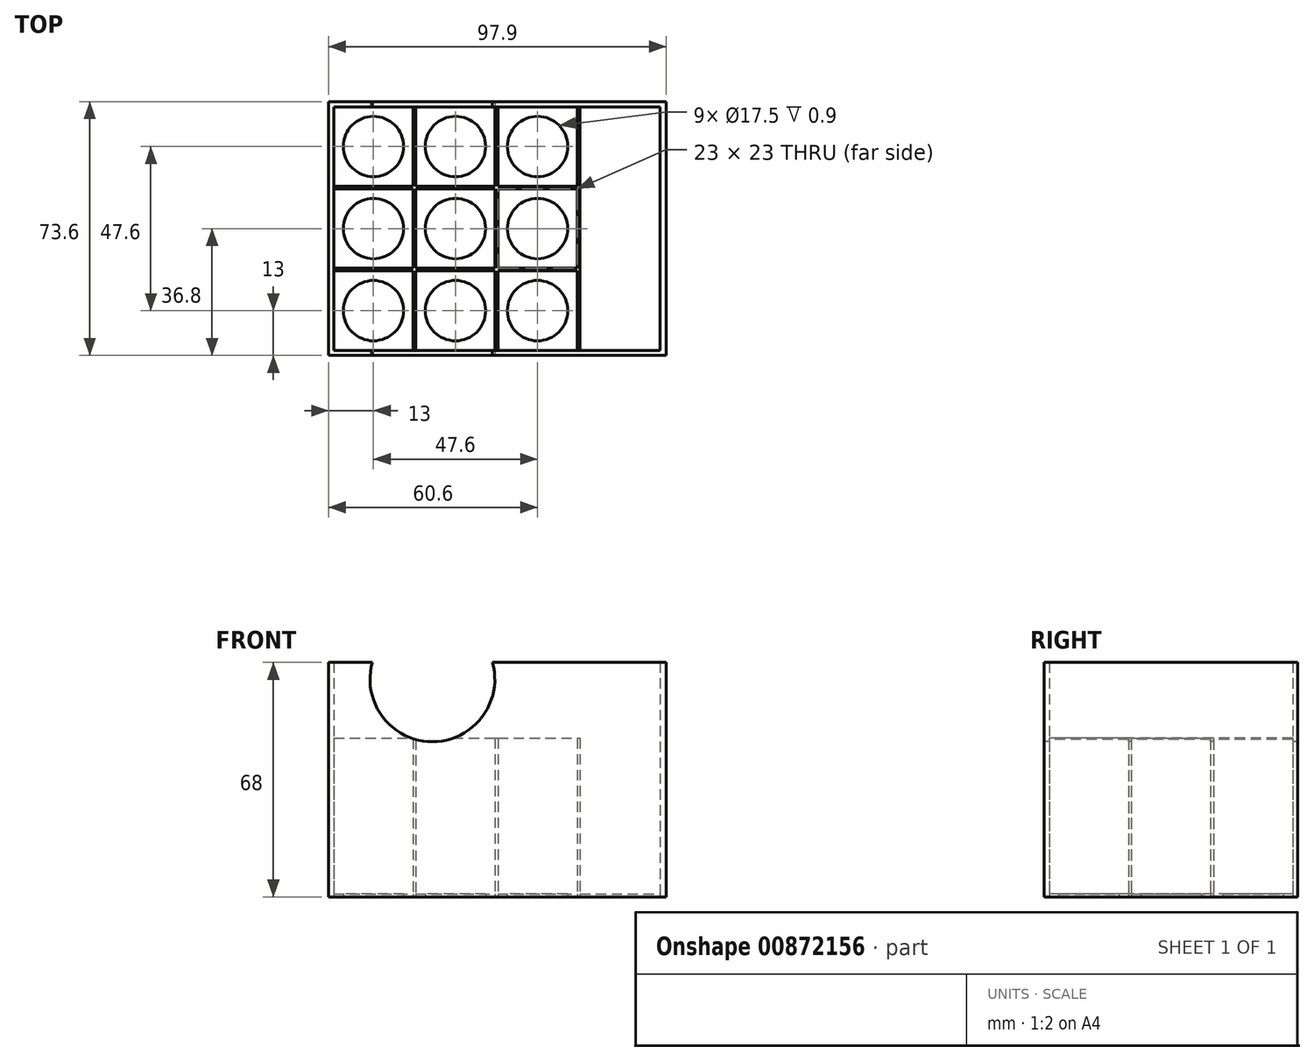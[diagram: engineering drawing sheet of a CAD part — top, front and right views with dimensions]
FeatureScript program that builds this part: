
annotation { "Feature Type Name" : "Feature", "Feature Type Description" : "" }
export const myFeature = defineFeature(function(context is Context, id is Id, definition is map)
    precondition{}
    {
        {
            var Q0;
            Q0=qCreatedBy(makeId("Top.planeOp"),FACE);
            var sketch = newSketch(context, id + "F0", { "sketchPlane" : qUnion([Q0])});
            skLineSegment(sketch, "E0.bottom", {"start": v(-48.95, 36.8) * mm, "end": v(48.95, 36.8) * mm});
            skLineSegment(sketch, "E0.top", {"start": v(-48.95, -36.8) * mm, "end": v(48.95, -36.8) * mm});
            skLineSegment(sketch, "E0.left", {"start": v(-48.95, 36.8) * mm, "end": v(-48.95, -36.8) * mm});
            skLineSegment(sketch, "E0.right", {"start": v(48.95, 36.8) * mm, "end": v(48.95, -36.8) * mm});
            skLineSegment(sketch, "E1", {"start": v(0, 53.1) * mm, "end": v(0, -59.16) * mm, "construction": true});
            skPoint(sketch, "E1.startSnap0", {"position": v(0, 36.8) * mm});
            skLineSegment(sketch, "E2", {"start": v(-56.88, 0) * mm, "end": v(64.17, 0) * mm, "construction": true});
            skPoint(sketch, "E2.startSnap0", {"position": v(-48.95, 0) * mm});
            skPoint(sketch, "E3", {"position": v(0, 0) * mm});
            skLineSegment(sketch, "E4", {"start": v(23.95, 35.3) * mm, "end": v(23.95, -35.3) * mm});
            skLineSegment(sketch, "E5.bottom", {"start": v(-47.45, 35.3) * mm, "end": v(-24.45, 35.3) * mm});
            skLineSegment(sketch, "E5.top", {"start": v(-47.45, 12.3) * mm, "end": v(-24.45, 12.3) * mm});
            skLineSegment(sketch, "E5.left", {"start": v(-47.45, 35.3) * mm, "end": v(-47.45, 12.3) * mm});
            skLineSegment(sketch, "E5.right", {"start": v(-24.45, 35.3) * mm, "end": v(-24.45, 12.3) * mm});
            skLineSegment(sketch, "E6.bottom", {"start": v(-23.65, 35.3) * mm, "end": v(-0.65, 35.3) * mm});
            skLineSegment(sketch, "E6.top", {"start": v(-23.65, 12.3) * mm, "end": v(-0.65, 12.3) * mm});
            skLineSegment(sketch, "E6.left", {"start": v(-23.65, 35.3) * mm, "end": v(-23.65, 12.3) * mm});
            skLineSegment(sketch, "E6.right", {"start": v(-0.65, 35.3) * mm, "end": v(-0.65, 12.3) * mm});
            skLineSegment(sketch, "E7.bottom", {"start": v(0.15, 35.3) * mm, "end": v(23.15, 35.3) * mm});
            skLineSegment(sketch, "E7.top", {"start": v(0.15, 12.3) * mm, "end": v(23.15, 12.3) * mm});
            skLineSegment(sketch, "E7.left", {"start": v(0.15, 35.3) * mm, "end": v(0.15, 12.3) * mm});
            skLineSegment(sketch, "E7.right", {"start": v(23.15, 35.3) * mm, "end": v(23.15, 12.3) * mm});
            skLineSegment(sketch, "E8", {"start": v(-54.63, 11.9) * mm, "end": v(61.76, 11.9) * mm, "construction": true});
            skLineSegment(sketch, "E9.MirrorCS", {"start": v(-23.65, -11.5) * mm, "end": v(-23.65, 11.5) * mm});
            skLineSegment(sketch, "E10.MirrorCS", {"start": v(23.15, -11.5) * mm, "end": v(23.15, 11.5) * mm});
            skLineSegment(sketch, "E11.MirrorCS", {"start": v(-47.45, -11.5) * mm, "end": v(-47.45, 11.5) * mm});
            skLineSegment(sketch, "E12.MirrorCS", {"start": v(0.15, -11.5) * mm, "end": v(23.15, -11.5) * mm});
            skLineSegment(sketch, "E13.MirrorCS", {"start": v(-47.45, -11.5) * mm, "end": v(-24.45, -11.5) * mm});
            skLineSegment(sketch, "E14.MirrorCS", {"start": v(-47.45, 11.5) * mm, "end": v(-24.45, 11.5) * mm});
            skLineSegment(sketch, "E15.MirrorCS", {"start": v(-0.65, -11.5) * mm, "end": v(-0.65, 11.5) * mm});
            skPoint(sketch, "E16.MirrorP", {"position": v(0, -13) * mm});
            skLineSegment(sketch, "E17.MirrorCS", {"start": v(-23.65, -11.5) * mm, "end": v(-0.65, -11.5) * mm});
            skLineSegment(sketch, "E18.MirrorCS", {"start": v(0.15, -11.5) * mm, "end": v(0.15, 11.5) * mm});
            skLineSegment(sketch, "E19.MirrorCS", {"start": v(0.15, 11.5) * mm, "end": v(23.15, 11.5) * mm});
            skLineSegment(sketch, "E20.MirrorCS", {"start": v(-24.45, -11.5) * mm, "end": v(-24.45, 11.5) * mm});
            skLineSegment(sketch, "E21.MirrorCS", {"start": v(-23.65, 11.5) * mm, "end": v(-0.65, 11.5) * mm});
            skLineSegment(sketch, "E22", {"start": v(-53.68, -11.9) * mm, "end": v(61.83, -11.9) * mm, "construction": true});
            skLineSegment(sketch, "E23.MirrorCS", {"start": v(-47.45, -12.3) * mm, "end": v(-47.45, -35.3) * mm});
            skLineSegment(sketch, "E24.MirrorCS", {"start": v(-47.45, -35.3) * mm, "end": v(-24.45, -35.3) * mm});
            skLineSegment(sketch, "E25.MirrorCS", {"start": v(-24.45, -12.3) * mm, "end": v(-24.45, -35.3) * mm});
            skLineSegment(sketch, "E26.MirrorCS", {"start": v(-47.45, -12.3) * mm, "end": v(-24.45, -12.3) * mm});
            skLineSegment(sketch, "E27.MirrorCS", {"start": v(-23.65, -12.3) * mm, "end": v(-23.65, -35.3) * mm});
            skLineSegment(sketch, "E28.MirrorCS", {"start": v(-23.65, -12.3) * mm, "end": v(-0.65, -12.3) * mm});
            skLineSegment(sketch, "E29.MirrorCS", {"start": v(-0.65, -12.3) * mm, "end": v(-0.65, -35.3) * mm});
            skLineSegment(sketch, "E30.MirrorCS", {"start": v(-23.65, -35.3) * mm, "end": v(-0.65, -35.3) * mm});
            skLineSegment(sketch, "E31.MirrorCS", {"start": v(0.15, -12.3) * mm, "end": v(0.15, -35.3) * mm});
            skLineSegment(sketch, "E32.MirrorCS", {"start": v(0.15, -12.3) * mm, "end": v(23.15, -12.3) * mm});
            skLineSegment(sketch, "E33.MirrorCS", {"start": v(23.15, -12.3) * mm, "end": v(23.15, -35.3) * mm});
            skLineSegment(sketch, "E34.MirrorCS", {"start": v(0.15, -35.3) * mm, "end": v(23.15, -35.3) * mm});
            skLineSegment(sketch, "E35", {"start": v(-51.69, 23.8) * mm, "end": v(-19.1, 23.8) * mm, "construction": true});
            skPoint(sketch, "E35.startSnap0", {"position": v(-47.45, 23.8) * mm});
            skLineSegment(sketch, "E36", {"start": v(-35.95, 38.92) * mm, "end": v(-35.95, 7.26) * mm, "construction": true});
            skPoint(sketch, "E36.startSnap0", {"position": v(-35.95, 35.3) * mm});
            skCircle(sketch, "E37", {"center": v(-35.95, 23.8) * mm, "radius": 8.75 * mm});
            skCircle(sketch, "E38.MirrorC", {"center": v(-35.95, 0) * mm, "radius": 8.75 * mm});
            skCircle(sketch, "E39.MirrorC", {"center": v(-35.95, -23.8) * mm, "radius": 8.75 * mm});
            skLineSegment(sketch, "E40", {"start": v(-24.05, -38.25) * mm, "end": v(-24.05, 39.3) * mm, "construction": true});
            skCircle(sketch, "E41.MirrorC", {"center": v(-12.15, 23.8) * mm, "radius": 8.75 * mm});
            skCircle(sketch, "E42.MirrorC", {"center": v(-12.15, 0) * mm, "radius": 8.75 * mm});
            skCircle(sketch, "E43.MirrorC", {"center": v(-12.15, -23.8) * mm, "radius": 8.75 * mm});
            skLineSegment(sketch, "E44", {"start": v(23.95, 35.3) * mm, "end": v(47.15, 35.3) * mm});
            skLineSegment(sketch, "E45", {"start": v(47.15, 35.3) * mm, "end": v(47.15, -35.3) * mm});
            skLineSegment(sketch, "E46", {"start": v(47.15, -35.3) * mm, "end": v(23.95, -35.3) * mm});
            skLineSegment(sketch, "E47", {"start": v(-47.45, 12.3) * mm, "end": v(-47.45, 11.5) * mm});
            skLineSegment(sketch, "E48", {"start": v(-24.45, 35.3) * mm, "end": v(-23.65, 35.3) * mm});
            skLineSegment(sketch, "E49", {"start": v(-0.65, 35.3) * mm, "end": v(0.15, 35.3) * mm});
            skLineSegment(sketch, "E50", {"start": v(23.15, 35.3) * mm, "end": v(23.95, 35.3) * mm});
            skLineSegment(sketch, "E51", {"start": v(23.15, -35.3) * mm, "end": v(23.95, -35.3) * mm});
            skLineSegment(sketch, "E52", {"start": v(-24.45, -35.3) * mm, "end": v(-23.65, -35.3) * mm});
            skLineSegment(sketch, "E53", {"start": v(-0.65, -35.3) * mm, "end": v(0.15, -35.3) * mm});
            skLineSegment(sketch, "E54", {"start": v(-0.25, 38.88) * mm, "end": v(-0.25, -45.6) * mm, "construction": true});
            skCircle(sketch, "E55.MirrorC", {"center": v(11.65, 23.8) * mm, "radius": 8.75 * mm});
            skCircle(sketch, "E56.MirrorC", {"center": v(11.65, 0) * mm, "radius": 8.75 * mm});
            skCircle(sketch, "E57.MirrorC", {"center": v(11.65, -23.8) * mm, "radius": 8.75 * mm});
            skLineSegment(sketch, "E58", {"start": v(-47.45, -11.5) * mm, "end": v(-47.45, -12.3) * mm});
            skLineSegment(sketch, "E59", {"start": v(23.55, 38.25) * mm, "end": v(23.55, -47.03) * mm, "construction": true});
            skLineSegment(sketch, "E60.MirrorCS", {"start": v(46.95, 35.3) * mm, "end": v(23.95, 35.3) * mm});
            skPoint(sketch, "E61.start.orphan", {"position": v(23.95, 12.3) * mm});
            skPoint(sketch, "E62.start.orphan", {"position": v(23.95, 11.5) * mm});
            skSolve(sketch);
        }
        {
            var Q0;
            Q0=makeQuery(id+"F0.imprint","IMPRINT",FACE,{"disambiguationData":[TD([[makeQuery(id+"F0.imprint","IMPRINT",EDGE,{"derivedFrom":sQuery(id+"F0.wireOp",EDGE,"E5.bottom")}),-1.0]])]});
            var Q1;
            Q1=makeQuery(id+"F0.imprint","IMPRINT",FACE,{"disambiguationData":[TD([[makeQuery(id+"F0.imprint","IMPRINT",EDGE,{"derivedFrom":sQuery(id+"F0.wireOp",EDGE,"E6.bottom")}),-1.0]])]});
            var Q2;
            Q2=makeQuery(id+"F0.imprint","IMPRINT",FACE,{"disambiguationData":[TD([[makeQuery(id+"F0.imprint","IMPRINT",EDGE,{"derivedFrom":sQuery(id+"F0.wireOp",EDGE,"E7.bottom")}),-1.0]])]});
            var Q3;
            {var subQ0=sQuery(id+"F0.wireOp",EDGE,"E44");Q3=makeQuery(id+"F0.imprint","IMPRINT",FACE,{"disambiguationData":[TD([[makeQuery(id+"F0.imprint","IMPRINT",EDGE,{"derivedFrom":subQ0}),-1.0]])]});}
            var Q4;
            Q4=makeQuery(id+"F0.imprint","IMPRINT",FACE,{"disambiguationData":[TD([[makeQuery(id+"F0.imprint","IMPRINT",EDGE,{"derivedFrom":sQuery(id+"F0.wireOp",EDGE,"E10.MirrorCS")}),1.0]])]});
            var Q5;
            Q5=makeQuery(id+"F0.imprint","IMPRINT",FACE,{"disambiguationData":[TD([[makeQuery(id+"F0.imprint","IMPRINT",EDGE,{"derivedFrom":sQuery(id+"F0.wireOp",EDGE,"E9.MirrorCS")}),-1.0]])]});
            var Q6;
            Q6=makeQuery(id+"F0.imprint","IMPRINT",FACE,{"disambiguationData":[TD([[makeQuery(id+"F0.imprint","IMPRINT",EDGE,{"derivedFrom":sQuery(id+"F0.wireOp",EDGE,"E11.MirrorCS")}),-1.0]])]});
            var Q7;
            Q7=makeQuery(id+"F0.imprint","IMPRINT",FACE,{"disambiguationData":[TD([[makeQuery(id+"F0.imprint","IMPRINT",EDGE,{"derivedFrom":sQuery(id+"F0.wireOp",EDGE,"E23.MirrorCS")}),1.0]])]});
            var Q8;
            Q8=makeQuery(id+"F0.imprint","IMPRINT",FACE,{"disambiguationData":[TD([[makeQuery(id+"F0.imprint","IMPRINT",EDGE,{"derivedFrom":sQuery(id+"F0.wireOp",EDGE,"E27.MirrorCS")}),1.0]])]});
            var Q9;
            Q9=makeQuery(id+"F0.imprint","IMPRINT",FACE,{"disambiguationData":[TD([[makeQuery(id+"F0.imprint","IMPRINT",EDGE,{"derivedFrom":sQuery(id+"F0.wireOp",EDGE,"E31.MirrorCS")}),1.0]])]});
            var Q10;
            {var subQ0=sQuery(id+"F0.wireOp",EDGE,"E46");Q10=makeQuery(id+"F0.imprint","IMPRINT",FACE,{"disambiguationData":[TD([[makeQuery(id+"F0.imprint","IMPRINT",EDGE,{"derivedFrom":subQ0}),-1.0]])]});}
            extrude(context, id + "F1", {"entities" : qUnion([Q0, Q1, Q2, Q3, Q4, Q5, Q6, Q7, Q8, Q9, Q10]), "depth" : .9 * mm, "offsetDistance" : 25 * mm});
        }
        {
            var Q0;
            Q0 = qSketchRegion(id + "F0", true);
            extrude(context, id + "F2", {"entities" : qUnion([Q0]), "depth" : (46 + 22) * mm, "offsetDistance" : 25 * mm});
        }
        {
            var Q0;
            Q0=makeQuery(id+"F0.imprint","IMPRINT",FACE,{"disambiguationData":[TD([[makeQuery(id+"F0.imprint","IMPRINT",EDGE,{"derivedFrom":sQuery(id+"F0.wireOp",EDGE,"E4")}),-1.0]])]});
            var Q1;
            {var subQ0=sQuery(id+"F0.wireOp",EDGE,"E61");Q1=makeQuery(id+"F0.imprint","IMPRINT",FACE,{"disambiguationData":[TD([[makeQuery(id+"F0.imprint","IMPRINT",EDGE,{"derivedFrom":subQ0}),-1.0]])]});}
            extrude(context, id + "F3", {"entities" : qUnion([Q0, Q1]), "depth" : 46 * mm, "offsetDistance" : 25 * mm});
        }
        {
            var Q0;
            Q0=makeQuery(id+"F2.opExtrude","SWEPT_FACE",FACE,{"disambiguationData":[OSD([sQuery(id+"F0.wireOp",EDGE,"E0.top")])]});
            var sketch = newSketch(context, id + "F4", { "sketchPlane" : qUnion([Q0])});
            skLineSegment(sketch, "E63", {"start": v(-53.2, 45) * mm, "end": v(59.52, 45) * mm, "construction": true});
            skArc(sketch, "E64", {"start": v(-36.27, 68) * mm, "mid": v(-18.85, 45) * mm, "end": v(-1.43, 68) * mm});
            skSolve(sketch);
        }
        {
            var Q0;
            {var subQ0=sQuery(id+"F4.wireOp",EDGE,"E64");Q0=makeQuery(id+"F4.imprint","IMPRINT",FACE,{"disambiguationData":[TD([[makeQuery(id+"F4.imprint","IMPRINT",EDGE,{"derivedFrom":subQ0}),1.0]])]});}
            extrude(context, id + "F5", {"entities" : qUnion([Q0]), "operationType" : NewBodyOperationType.REMOVE, "oppositeDirection" : true, "depth" : 100 * mm, "offsetDistance" : 25 * mm});
        }
    });
